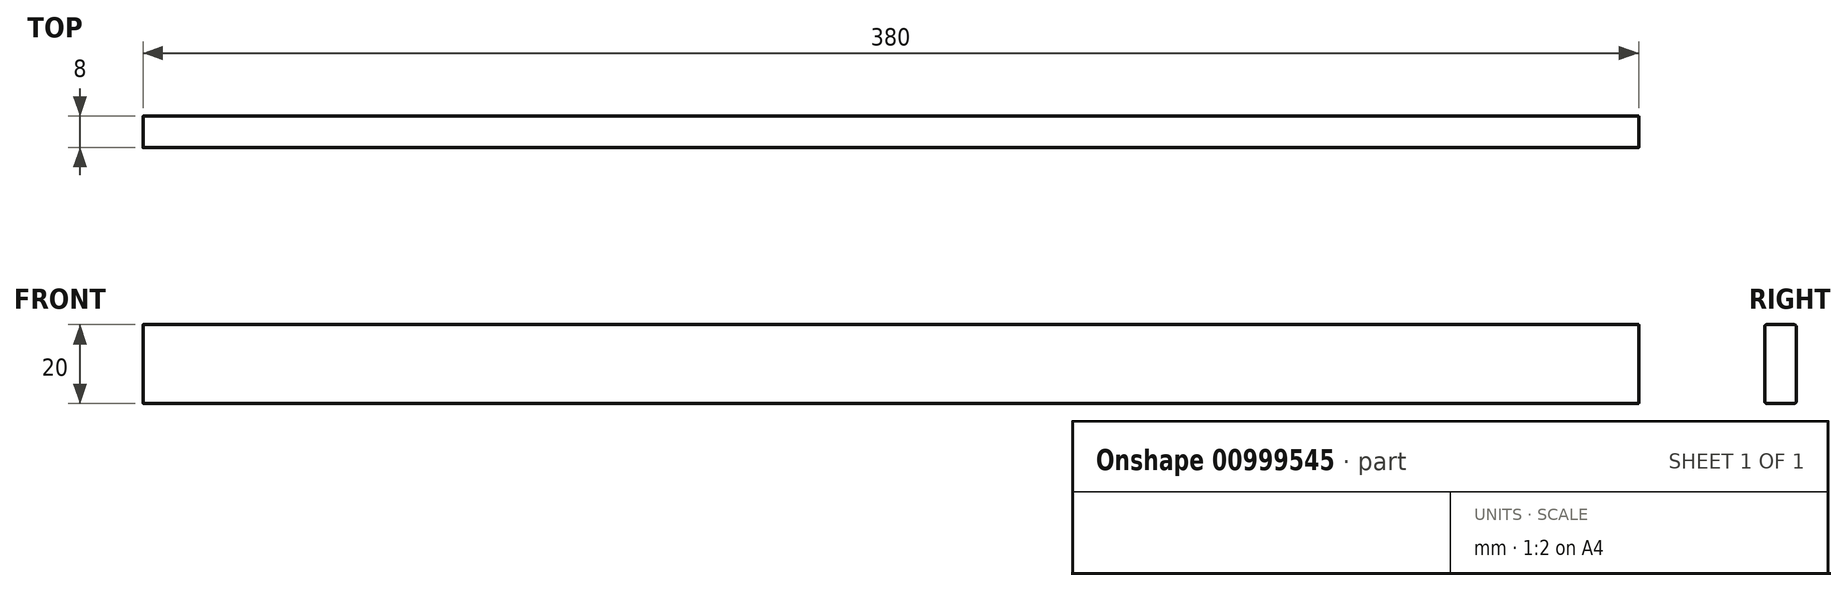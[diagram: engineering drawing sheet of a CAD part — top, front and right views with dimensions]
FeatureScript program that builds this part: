
annotation { "Feature Type Name" : "Feature", "Feature Type Description" : "" }
export const myFeature = defineFeature(function(context is Context, id is Id, definition is map)
    precondition{}
    {
        {
            var Q0;
            Q0=qCreatedBy(makeId("Front.planeOp"),FACE);
            var sketch = newSketch(context, id + "F0", { "sketchPlane" : qUnion([Q0]), "disableImprinting" : false});
            skLineSegment(sketch, "E0.bottom", {"start": v(-190, 10) * mm, "end": v(190, 10) * mm});
            skLineSegment(sketch, "E0.top", {"start": v(-190, -10) * mm, "end": v(190, -10) * mm});
            skLineSegment(sketch, "E0.left", {"start": v(-190, 10) * mm, "end": v(-190, -10) * mm});
            skLineSegment(sketch, "E0.right", {"start": v(190, 10) * mm, "end": v(190, -10) * mm});
            skPoint(sketch, "E0.middle", {"position": v(0, 0) * mm});
            skSolve(sketch);
        }
        {
            var Q0;
            Q0=makeQuery(id+"F0.imprint","IMPRINT",FACE,{"disambiguationData":[TD([[makeQuery(id+"F0.imprint","IMPRINT",EDGE,{"derivedFrom":sQuery(id+"F0.wireOp",EDGE,"E0.bottom")}),-1.0]])]});
            extrude(context, id + "F1", {"entities" : qUnion([Q0]), "flatOperationType" : FlatOperationType.REMOVE, "thickness1" : 5 * mm, "thickness2" : 0 * mm, "thickness" : 5 * mm, "depth" : 8 * mm, "offsetDistance" : 25 * mm, "startOffsetBound" : StartOffsetType.BLIND, "startOffsetDistance" : 25 * mm, "domain" : OperationDomain.MODEL});
        }
        {
            var Q0;
            Q0=makeQuery(id+"F1.opExtrude","CAP_EDGE",EDGE,{"disambiguationData":[OSD([sQuery(id+"F0.wireOp",EDGE,"E0.bottom")])],"isStart":false});
            var Q1;
            Q1=makeQuery(id+"F1.opExtrude","CAP_EDGE",EDGE,{"disambiguationData":[OSD([sQuery(id+"F0.wireOp",EDGE,"E0.bottom")])],"isStart":true});
            var Q2;
            Q2=makeQuery(id+"F1.opExtrude","CAP_EDGE",EDGE,{"disambiguationData":[OSD([sQuery(id+"F0.wireOp",EDGE,"E0.top")])],"isStart":true});
            var Q3;
            Q3=makeQuery(id+"F1.opExtrude","CAP_EDGE",EDGE,{"disambiguationData":[OSD([sQuery(id+"F0.wireOp",EDGE,"E0.top")])],"isStart":false});
            fillet(context, id + "F2", {"entities" : qUnion([Q0, Q1, Q2, Q3]), "radius" : 0.5 * mm, "width" : 5 * mm, "tangentPropagation" : true, "blendControlType" : BlendControlType.RADIUS, "defaultsChanged" : false, "isAsymmetric" : false, "otherRadius" : 5 * mm, "flipAsymmetric" : false, "isPartial" : false, "partialFirstEdgeTotalParameter" : 0.01, "partialOppositeParameter" : true, "secondBound" : false, "partialSecondEdgeTotalParameter" : 0.99, "vertexSettings" : [], "pointOnEdgeSettings" : [], "allowEdgeOverflow" : false, "smoothCorners" : false, "filletType" : FilletType.EDGE});
        }
    });
